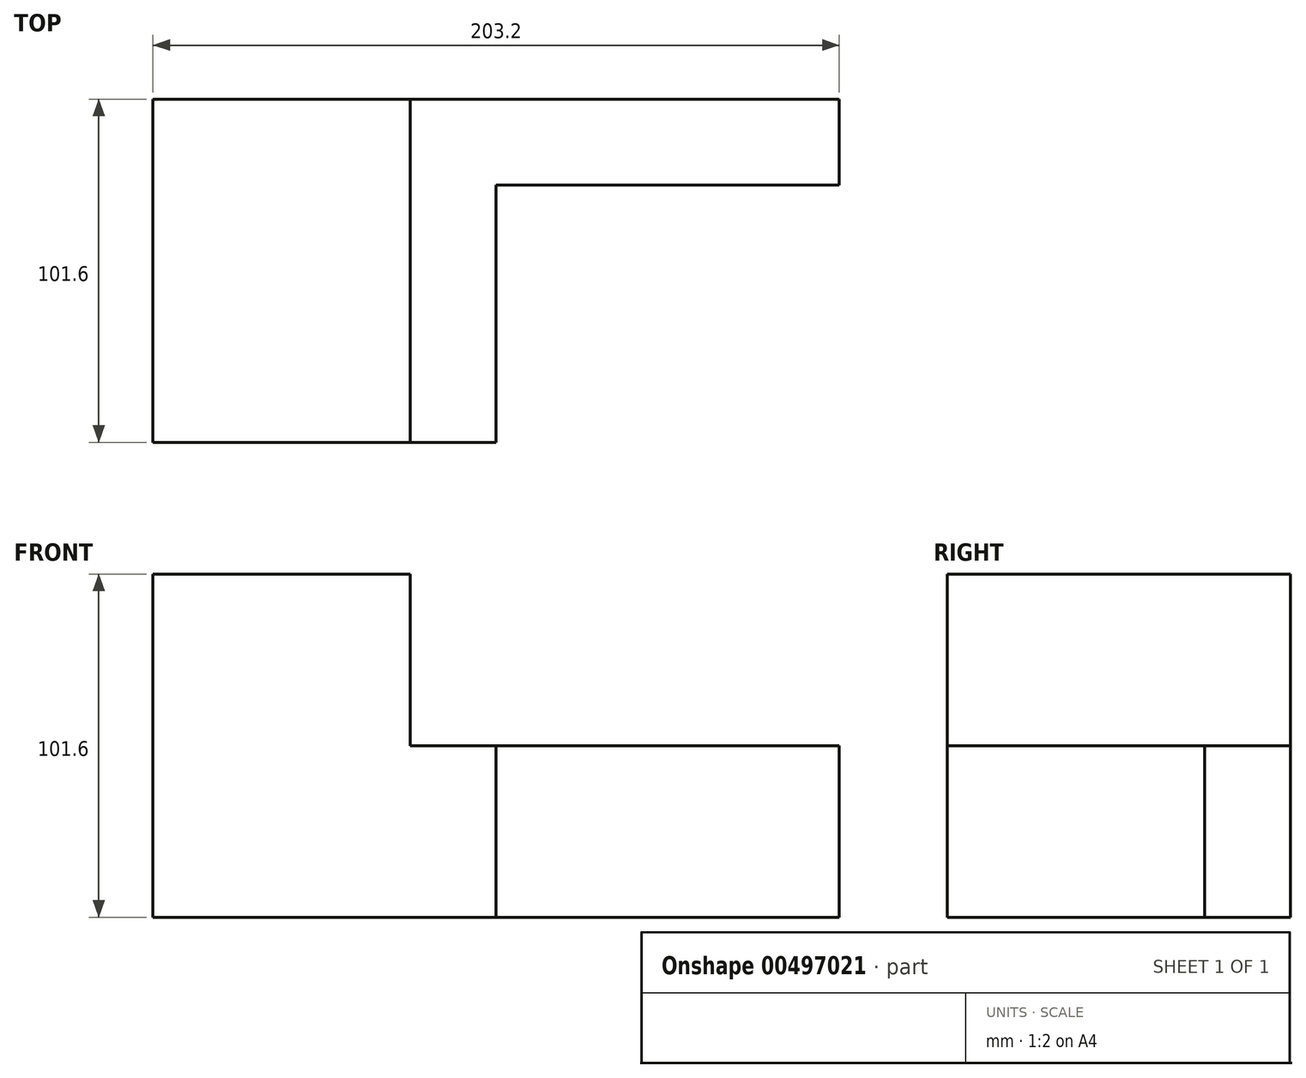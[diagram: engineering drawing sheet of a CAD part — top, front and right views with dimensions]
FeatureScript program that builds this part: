
annotation { "Feature Type Name" : "Feature", "Feature Type Description" : "" }
export const myFeature = defineFeature(function(context is Context, id is Id, definition is map)
    precondition{}
    {
        {
            var Q0;
            Q0=qCreatedBy(makeId("Front.planeOp"),FACE);
            var sketch = newSketch(context, id + "F0", { "sketchPlane" : qUnion([Q0])});
            skLineSegment(sketch, "E0.bottom", {"start": v(0, 0) * mm, "end": v(101.6, 0) * mm});
            skLineSegment(sketch, "E0.top", {"start": v(0, 101.6) * mm, "end": v(76.2, 101.6) * mm});
            skLineSegment(sketch, "E0.left", {"start": v(0, 0) * mm, "end": v(0, 101.6) * mm});
            skLineSegment(sketch, "E1", {"start": v(0, 50.8) * mm, "end": v(76.2, 50.8) * mm});
            skPoint(sketch, "E1.endSnap0", {"position": v(0, 50.8) * mm});
            skLineSegment(sketch, "E2", {"start": v(76.2, 50.8) * mm, "end": v(76.2, 101.6) * mm});
            skLineSegment(sketch, "E3", {"start": v(76.2, 50.8) * mm, "end": v(101.6, 50.8) * mm});
            skLineSegment(sketch, "E4", {"start": v(101.6, 50.8) * mm, "end": v(101.6, 0) * mm});
            skLineSegment(sketch, "E5", {"start": v(101.6, 50.8) * mm, "end": v(203.2, 50.8) * mm});
            skPoint(sketch, "E6.orphan", {"position": v(203.2, 0) * mm});
            skLineSegment(sketch, "E7", {"start": v(203.2, 50.8) * mm, "end": v(203.2, 0) * mm});
            skLineSegment(sketch, "E8", {"start": v(101.6, 0) * mm, "end": v(203.2, 0) * mm});
            skPoint(sketch, "E0.right.end.orphan", {"position": v(203.2, 101.6) * mm});
            skLineSegment(sketch, "E9", {"start": v(76.2, 50.8) * mm, "end": v(76.2, 0) * mm});
            skSolve(sketch);
        }
        {
            var Q0;
            {var subQ4=sQuery(id+"F0.wireOp",EDGE,"E1");Q0=makeQuery(id+"F0.imprint","IMPRINT",FACE,{"disambiguationData":[TD([[makeQuery(id+"F0.imprint","IMPRINT",EDGE,{"derivedFrom":subQ4}),1.0]])]});}
            var Q1;
            {var subQ1=sQuery(id+"F0.wireOp",EDGE,"E0.bottom");Q1=makeQuery(id+"F0.imprint","IMPRINT",FACE,{"disambiguationData":[TD([[makeQuery(id+"F0.imprint","IMPRINT",EDGE,{"derivedFrom":subQ1}),1.0]])]});}
            extrude(context, id + "F1", {"entities" : qUnion([Q0, Q1]), "oppositeDirection" : true, "depth" : 101.6 * mm});
        }
        {
            var Q0;
            Q0=makeQuery(id+"F0.imprint","IMPRINT",FACE,{"disambiguationData":[TD([[makeQuery(id+"F0.imprint","IMPRINT",EDGE,{"derivedFrom":sQuery(id+"F0.wireOp",EDGE,"E4")}),1.0]])]});
            extrude(context, id + "F2", {"entities" : qUnion([Q0]), "operationType" : NewBodyOperationType.ADD, "oppositeDirection" : true, "depth" : 101.6 * mm, "hasSecondDirection" : true, "secondDirectionOppositeDirection" : true, "secondDirectionDepth" : 76.2 * mm});
        }
    });
